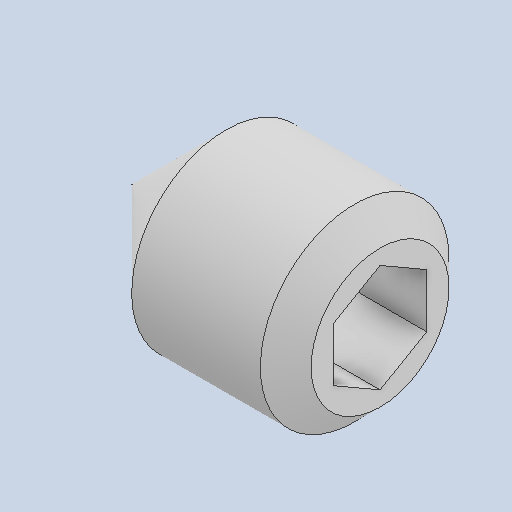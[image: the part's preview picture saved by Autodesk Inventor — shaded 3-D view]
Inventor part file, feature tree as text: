
AUTODESK INVENTOR PART (.ipt)
format: ipt  version: 2022 (Build 260153000, 153)  size: 108,544 bytes
history: native  units: in
note: dims shown in document units (in); Inventor stores cm internally (conversion verified against a paired STEP export)
features: chamfer x1
ambient origin geometry x8: Origin, YZ Plane, XZ Plane, XY Plane, X Axis, Y Axis, Z Axis, Center Point
bodies: Solid1 (feature_tree)
feature tree (1):
  chamfer  "Chamfer2"  [1 undecoded]
note: 1 required parameter value undecoded (feature->parameter linkage not recoverable at this tier; creation-order binding heuristic only, values carry confidence <= 0.55)
